# Revit family: Storage-Teknion-PCSS_Stockholm-R20153
name_source: partatom
category: Furniture
revit_build: Autodesk Revit Architecture 2015 (Build: 20140323_1530(x64)
units: mm (PartAtom-declared; Revit-internal decimal feet)

## types (5) — shared parameters
Assembly Code = E2020200
Manufacturer = Teknion
Manufacturer Fax = 416.661.4586
Part Number = PCSS
Product Documentation Link = https://d2r72yk5wmppdj.cloudfront.net
Product Line = Punt Collection
Product Page URL = https://www.teknion.com
Series = Punt Collection
Sustainability Data = http://www.teknion.com
URL = www.teknion.com
Unit Weight URL = http://www.teknion.com
Warranty = http://www.teknion.com

## per-type parameters (varying)
| type | Back Cut Hole Depth | Back Visibility | Description | Has Base | Has No Base | Height | Model | Wall Mounted |
| With Base, Standard Back, 31" High | 3.744 " | Yes | Stockholm Storage, with Base, Standard Back, 31" Height | Yes | No | 11.524 " | PCSSB__ | No |
| No Base, Standard Back, 20" High | 3.744 " | Yes | Stockholm Storage, No Base, Standard Back, 20" Height | No | Yes | 0.5 " | PCSSS__ | No |
| Wall Mounted, 20" High Case | 3.744 " | Yes | Stockholm Storage, Wall Mounted, 20" High Case | No | No | 11.524 " | PCSSM__ | Yes |
| With Base, Finished Back, 31" High | 2 " | No | Stockholm Storage, with Base, Finished Back, 31" Height | Yes | No | 11.524 " | PCSSW__ | No |
| No Base, Finished Back, 20" High | 2 " | No | Stockholm Storage, No Base, Finished Back, 20" Height | No | Yes | 0.5 " | PCSSF__ | No |

## geometry (parser evidence)
native form markers: Sweep x2
no freeform markers — native parametric forms only
